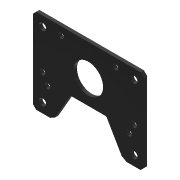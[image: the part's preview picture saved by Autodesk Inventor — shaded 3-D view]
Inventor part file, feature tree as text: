
AUTODESK INVENTOR PART (.ipt)
format: ipt  version: 2013 (Build 170138000, 138)  size: 100,864 bytes
history: native  units: in
note: dims shown in document units (in); Inventor stores cm internally (conversion verified against a paired STEP export)
features: fillet x1, other x1, imported_body x1
ambient origin geometry x8: Origin, YZ Plane, XZ Plane, XY Plane, X Axis, Y Axis, Z Axis, Center Point
feature tree (3):
  fillet  "Fillet1"  [1 undecoded]
  other  "217-2617-001 Rev41"
  imported_body  "Base1"
note: 1 required parameter value undecoded (feature->parameter linkage not recoverable at this tier; creation-order binding heuristic only, values carry confidence <= 0.55)
